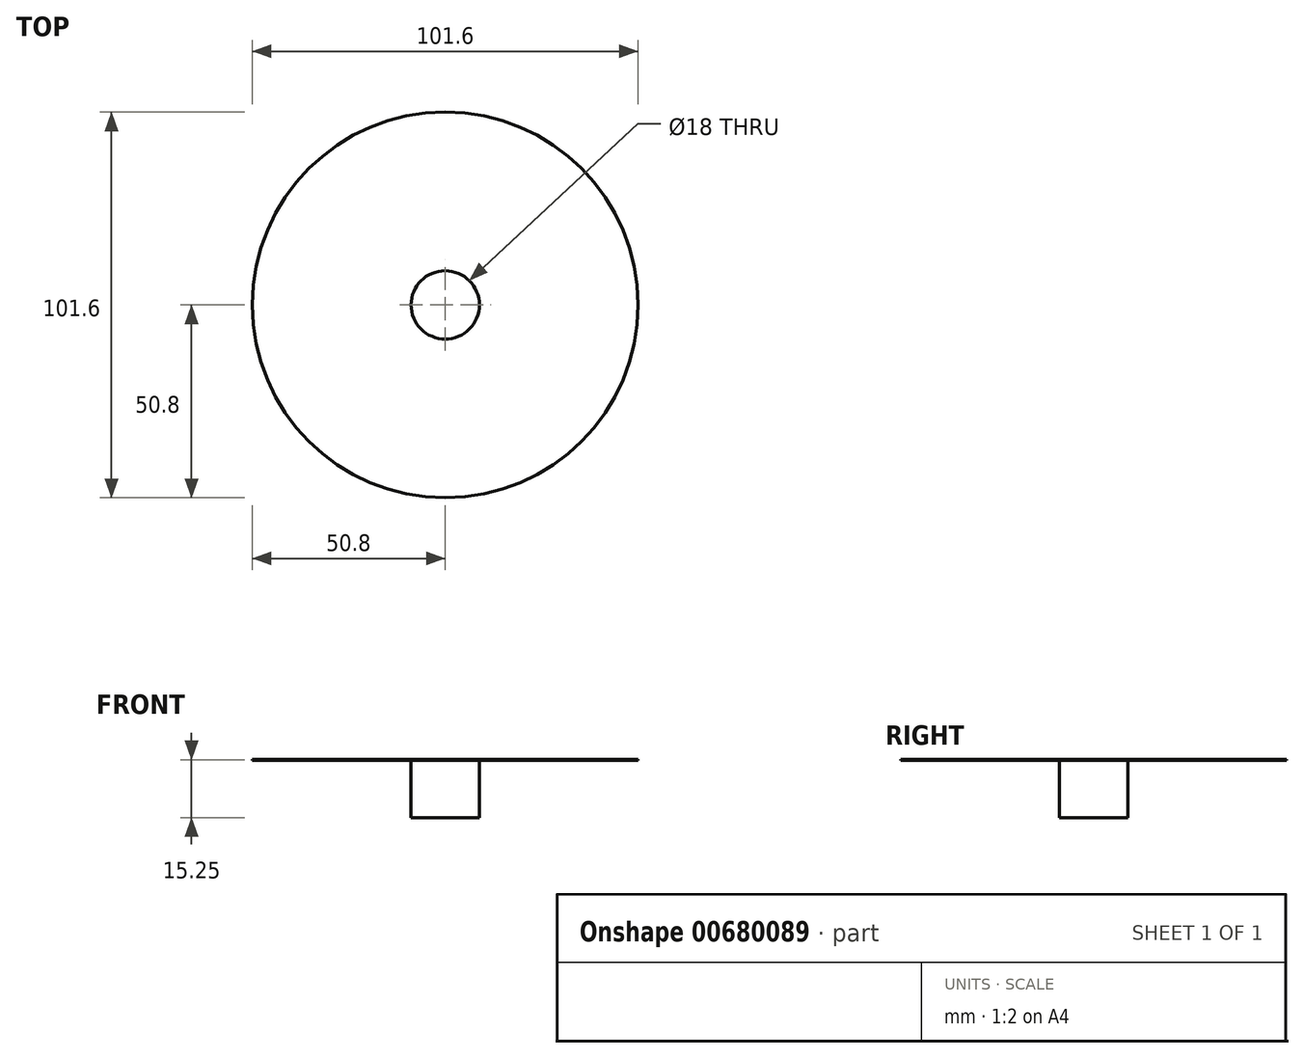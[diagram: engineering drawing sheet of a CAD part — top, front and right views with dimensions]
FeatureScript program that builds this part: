
annotation { "Feature Type Name" : "Feature", "Feature Type Description" : "" }
export const myFeature = defineFeature(function(context is Context, id is Id, definition is map)
    precondition{}
    {
        {
            var Q0;
            Q0=qCreatedBy(makeId("Top.planeOp"),FACE);
            var sketch = newSketch(context, id + "F0", { "sketchPlane" : qUnion([Q0])});
            skCircle(sketch, "E0", {"center": v(0, 0) * mm, "radius": 9 * mm});
            skSolve(sketch);
        }
        {
            var Q0;
            Q0=makeQuery(id+"F0.imprint","IMPRINT",FACE,{"disambiguationData":[TD([[makeQuery(id+"F0.imprint","IMPRINT",EDGE,{"derivedFrom":sQuery(id+"F0.wireOp",EDGE,"E0")}),1.0]])]});
            extrude(context, id + "F1", {"entities" : qUnion([Q0]), "depth" : 15 * mm, "offsetDistance" : 25.4 * mm});
        }
        {
            var Q0;
            Q0=makeQuery(id+"F1.opExtrude","CAP_FACE",FACE,{"disambiguationData":[OSD([sQuery(id+"F0.wireOp",EDGE,"E0")])],"isStart":false});
            var sketch = newSketch(context, id + "F2", { "sketchPlane" : qUnion([Q0])});
            skCircle(sketch, "E1", {"center": v(0, 0) * mm, "radius": 50.8 * mm});
            skSolve(sketch);
        }
        {
            var Q0;
            Q0=makeQuery(id+"F2.imprint","IMPRINT",FACE,{"disambiguationData":[TD([[makeQuery(id+"F2.imprint","IMPRINT",EDGE,{"derivedFrom":sQuery(id+"F2.wireOp",EDGE,"E1")}),1.0]])]});
            extrude(context, id + "F3", {"entities" : qUnion([Q0]), "depth" : 0.25 * mm, "offsetDistance" : 25.4 * mm});
        }
    });
